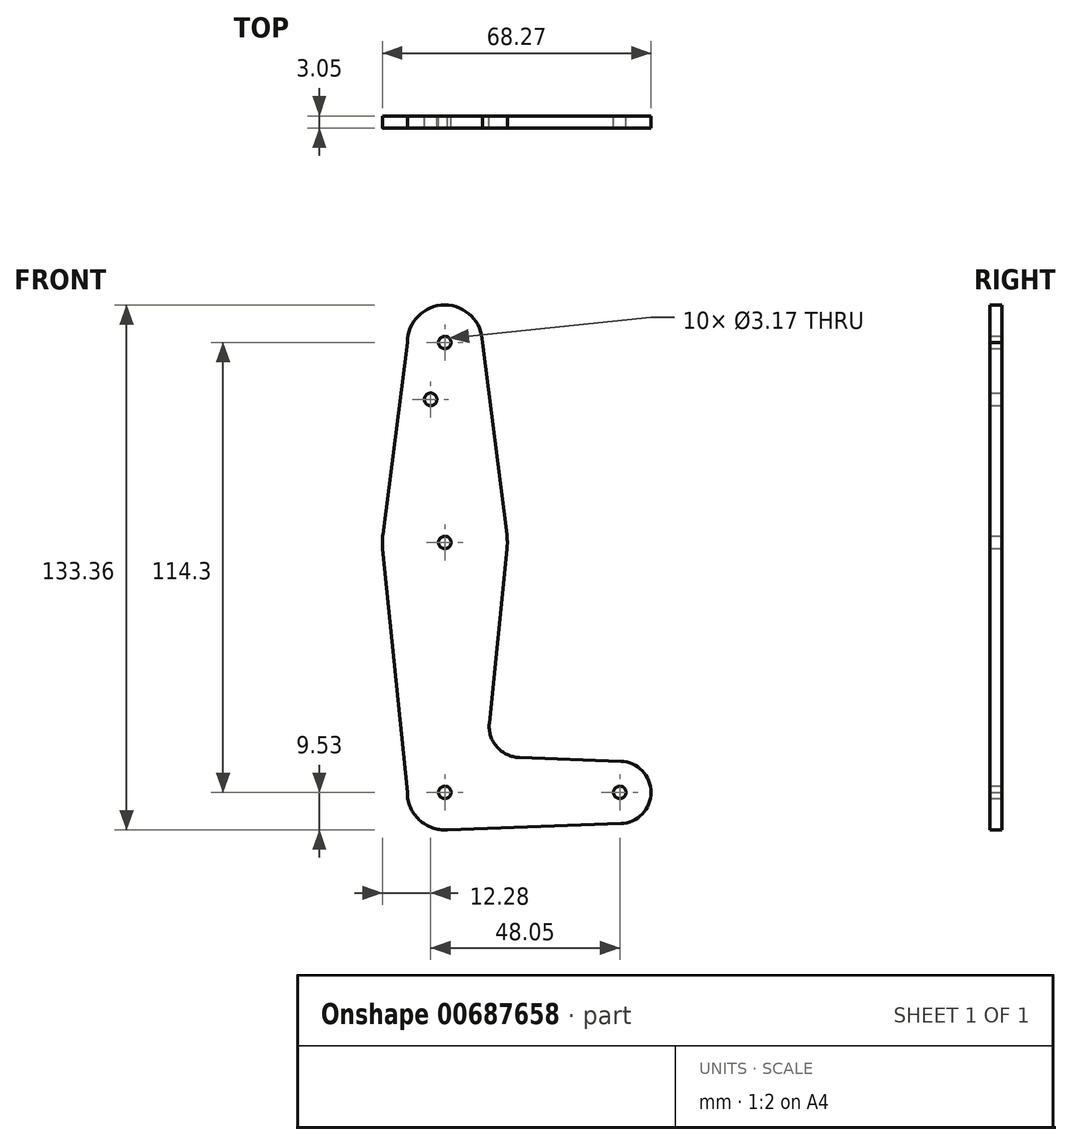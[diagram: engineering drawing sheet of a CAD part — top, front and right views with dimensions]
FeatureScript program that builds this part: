
annotation { "Feature Type Name" : "Feature", "Feature Type Description" : "" }
export const myFeature = defineFeature(function(context is Context, id is Id, definition is map)
    precondition{}
    {
        {
            var Q0;
            Q0=qCreatedBy(makeId("Front.planeOp"),FACE);
            var sketch = newSketch(context, id + "F0", { "sketchPlane" : qUnion([Q0])});
            skLineSegment(sketch, "E0", {"start": v(0, 114.3) * mm, "end": v(0, 0) * mm});
            skLineSegment(sketch, "E1", {"start": v(0, 0) * mm, "end": v(44.45, 0) * mm});
            skCircle(sketch, "E2", {"center": v(0, 114.3) * mm, "radius": 9.53 * mm});
            skCircle(sketch, "E3", {"center": v(0, 63.5) * mm, "radius": 15.88 * mm});
            skCircle(sketch, "E4", {"center": v(0, 0) * mm, "radius": 9.53 * mm});
            skCircle(sketch, "E5", {"center": v(44.45, 0) * mm, "radius": 7.94 * mm});
            skLineSegment(sketch, "E6", {"start": v(-9.53, 0) * mm, "end": v(-15.8, 61.9) * mm});
            skLineSegment(sketch, "E7", {"start": v(-9.53, 114.3) * mm, "end": v(-15.75, 65.5) * mm});
            skLineSegment(sketch, "E8", {"start": v(15.75, 65.5) * mm, "end": v(9.52, 114.3) * mm});
            skLineSegment(sketch, "E9", {"start": v(15.8, 61.9) * mm, "end": v(11.3, 17.6) * mm});
            skLineSegment(sketch, "E10", {"start": v(0, -9.53) * mm, "end": v(44.73, -7.93) * mm});
            skLineSegment(sketch, "E11", {"start": v(18.93, 8.85) * mm, "end": v(44.73, 7.93) * mm});
            skCircle(sketch, "E12", {"center": v(0, 114.3) * mm, "radius": 1.59 * mm});
            skCircle(sketch, "E13", {"center": v(0, 63.5) * mm, "radius": 1.59 * mm});
            skCircle(sketch, "E14", {"center": v(0, 0) * mm, "radius": 1.59 * mm});
            skCircle(sketch, "E15", {"center": v(44.45, 0) * mm, "radius": 1.59 * mm});
            skCircle(sketch, "E16", {"center": v(-3.6, 99.85) * mm, "radius": 1.59 * mm});
            skArc(sketch, "E17.filletArc", {"start": v(11.3, 17.6) * mm, "mid": v(13.22, 11.57) * mm, "end": v(18.93, 8.85) * mm});
            skSolve(sketch);
        }
        {
            var Q0;
            Q0 = qSketchRegion(id + "F0", true);
            var Q1;
            {var subQ0=sQuery(id+"F0.wireOp",EDGE,"E4");var subQ1=sQuery(id+"F0.wireOp",EDGE,"E0");var subQ2=makeQuery(id+"F0.imprint","INTERSECT",VERTEX,{"derivedFrom":[subQ1,subQ0]});Q1=makeQuery(id+"F0.imprint","IMPRINT",FACE,{"disambiguationData":[TD([[makeQuery(id+"F0.imprint","IMPRINT",EDGE,{"disambiguationData":[TD([[subQ2,-1.0]])],"derivedFrom":subQ1}),1.0]])]});}
            extrude(context, id + "F1", {"entities" : qUnion([Q0, Q1]), "depth" : 3.05 * mm, "offsetDistance" : 25.4 * mm});
        }
    });
